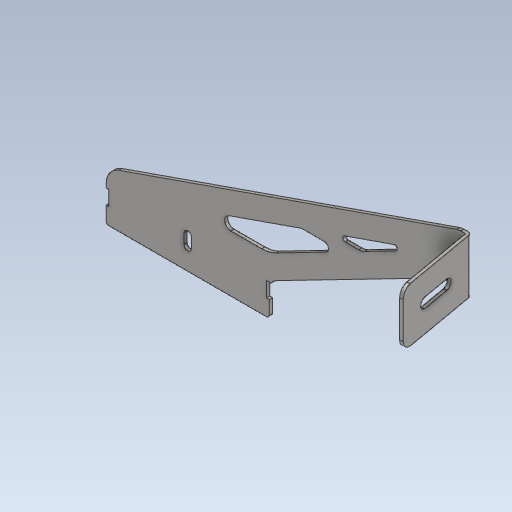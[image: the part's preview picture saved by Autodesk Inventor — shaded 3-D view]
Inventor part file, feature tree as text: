
AUTODESK INVENTOR PART (.ipt)
format: ipt  version: 2020 (Build 240168000, 168)  size: 203,776 bytes
history: native  units: mm
features: other x4, sketch x1, plane x1
ambient origin geometry x8: Origin, YZ Plane, XZ Plane, XY Plane, X Axis, Y Axis, Z Axis, Center Point
bodies: Body1 (feature_tree)
feature tree (6):
  other  "吊架-長(R)(#11.26).ipt"
  other  "實體1::吊架-長(R)(#11.26).ipt"
  other  "標籤特徵1"
  sketch  "草圖1"
  plane  "工作平面1"
  other  "實體1"
